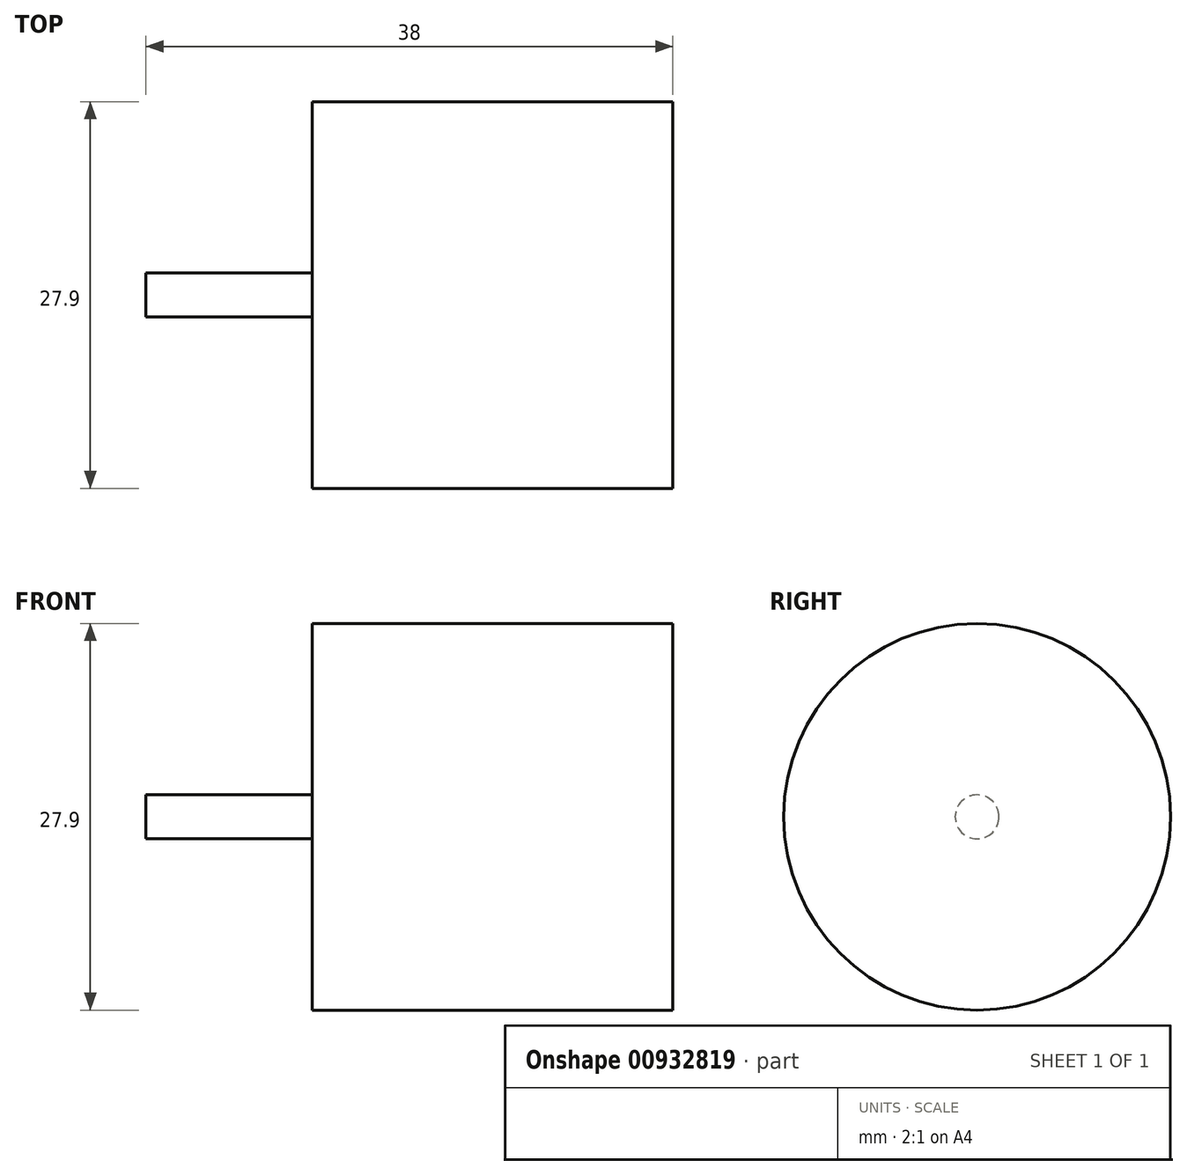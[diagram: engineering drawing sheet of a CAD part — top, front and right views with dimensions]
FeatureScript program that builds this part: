
annotation { "Feature Type Name" : "Feature", "Feature Type Description" : "" }
export const myFeature = defineFeature(function(context is Context, id is Id, definition is map)
    precondition{}
    {
        {
            var Q0;
            Q0=qCreatedBy(makeId("Right.planeOp"),FACE);
            var sketch = newSketch(context, id + "F0", { "sketchPlane" : qUnion([Q0])});
            skCircle(sketch, "E0", {"center": v(0, 0) * mm, "radius": 13.95 * mm});
            skSolve(sketch);
        }
        {
            var Q0;
            Q0=makeQuery(id+"F0.imprint","IMPRINT",FACE,{"disambiguationData":[TD([[makeQuery(id+"F0.imprint","IMPRINT",EDGE,{"derivedFrom":sQuery(id+"F0.wireOp",EDGE,"E0")}),1.0]])]});
            extrude(context, id + "F1", {"entities" : qUnion([Q0]), "depth" : 26 * mm, "offsetDistance" : 25 * mm});
        }
        {
            var Q0;
            Q0=makeQuery(id+"F1.opExtrude","CAP_FACE",FACE,{"disambiguationData":[OSD([sQuery(id+"F0.wireOp",EDGE,"E0")])],"isStart":true});
            var sketch = newSketch(context, id + "F2", { "sketchPlane" : qUnion([Q0])});
            skCircle(sketch, "E1", {"center": v(0, 0) * mm, "radius": 1.58 * mm});
            skSolve(sketch);
        }
        {
            var Q0;
            Q0=makeQuery(id+"F2.imprint","IMPRINT",FACE,{"disambiguationData":[TD([[makeQuery(id+"F2.imprint","IMPRINT",EDGE,{"derivedFrom":sQuery(id+"F2.wireOp",EDGE,"E1")}),1.0]])]});
            extrude(context, id + "F3", {"entities" : qUnion([Q0]), "operationType" : NewBodyOperationType.ADD, "depth" : 12 * mm, "offsetDistance" : 25 * mm});
        }
    });
